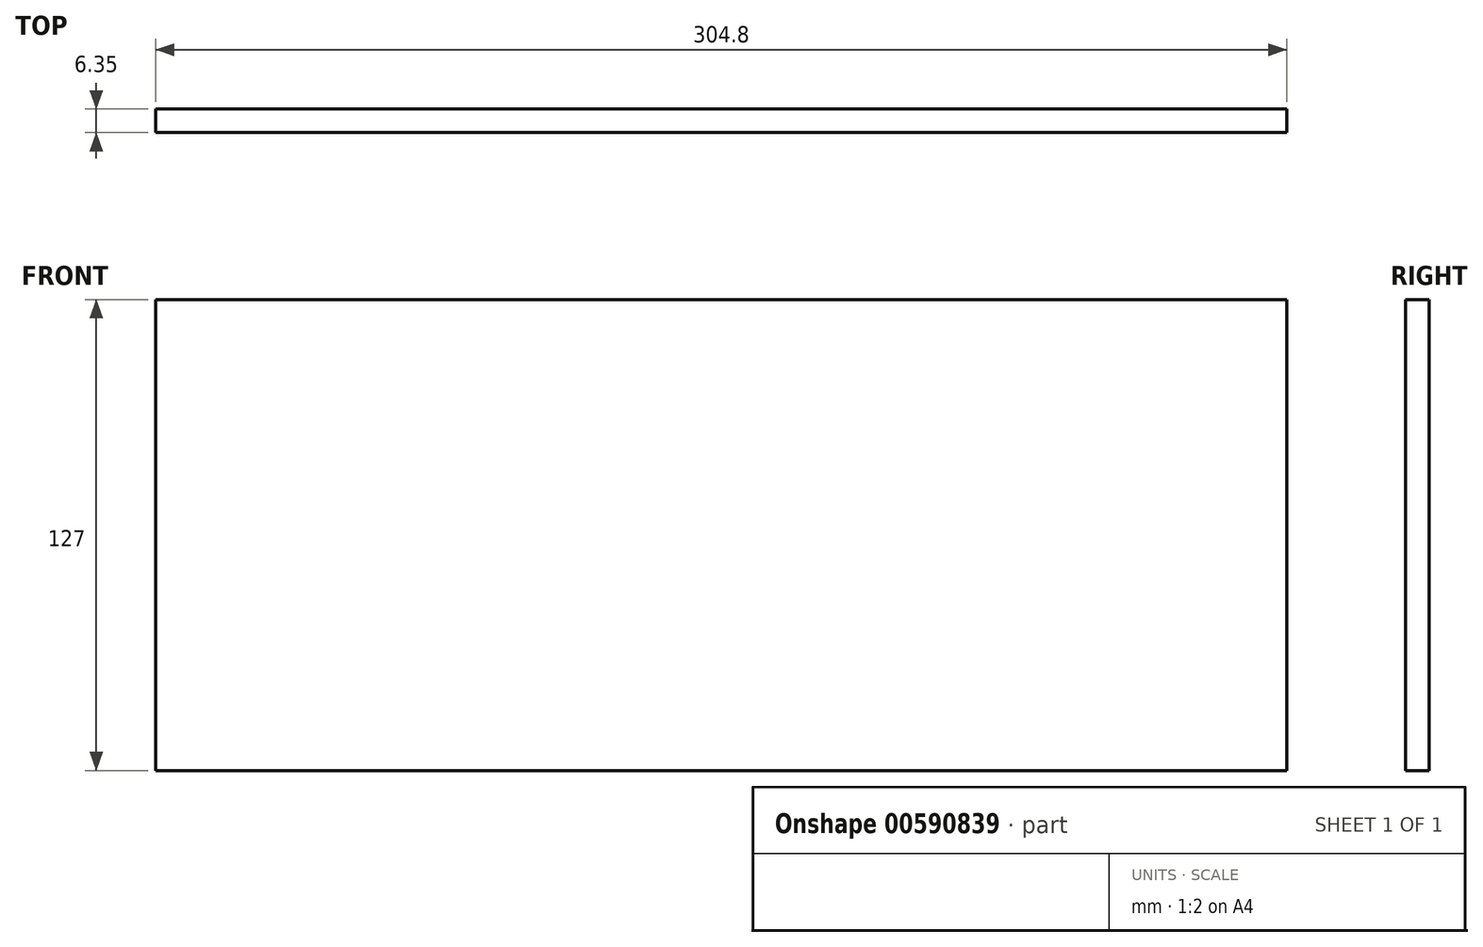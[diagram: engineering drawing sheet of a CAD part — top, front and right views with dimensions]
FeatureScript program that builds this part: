
annotation { "Feature Type Name" : "Feature", "Feature Type Description" : "" }
export const myFeature = defineFeature(function(context is Context, id is Id, definition is map)
    precondition{}
    {
        {
            var Q0;
            Q0=qCreatedBy(makeId("Front.planeOp"),FACE);
            var sketch = newSketch(context, id + "F0", { "sketchPlane" : qUnion([Q0])});
            skLineSegment(sketch, "E0.bottom", {"start": v(137, -10.93) * mm, "end": v(-167.8, -10.93) * mm});
            skLineSegment(sketch, "E0.top", {"start": v(137, -137.93) * mm, "end": v(-167.8, -137.93) * mm});
            skLineSegment(sketch, "E0.left", {"start": v(137, -10.93) * mm, "end": v(137, -137.93) * mm});
            skLineSegment(sketch, "E0.right", {"start": v(-167.8, -10.93) * mm, "end": v(-167.8, -137.93) * mm});
            skSolve(sketch);
        }
        {
            var Q0;
            Q0=makeQuery(id+"F0.imprint","IMPRINT",FACE,{"disambiguationData":[TD([[makeQuery(id+"F0.imprint","IMPRINT",EDGE,{"derivedFrom":sQuery(id+"F0.wireOp",EDGE,"E0.bottom")}),1.0]])]});
            extrude(context, id + "F1", {"entities" : qUnion([Q0]), "depth" : 6.35 * mm, "offsetDistance" : 25.4 * mm});
        }
    });
